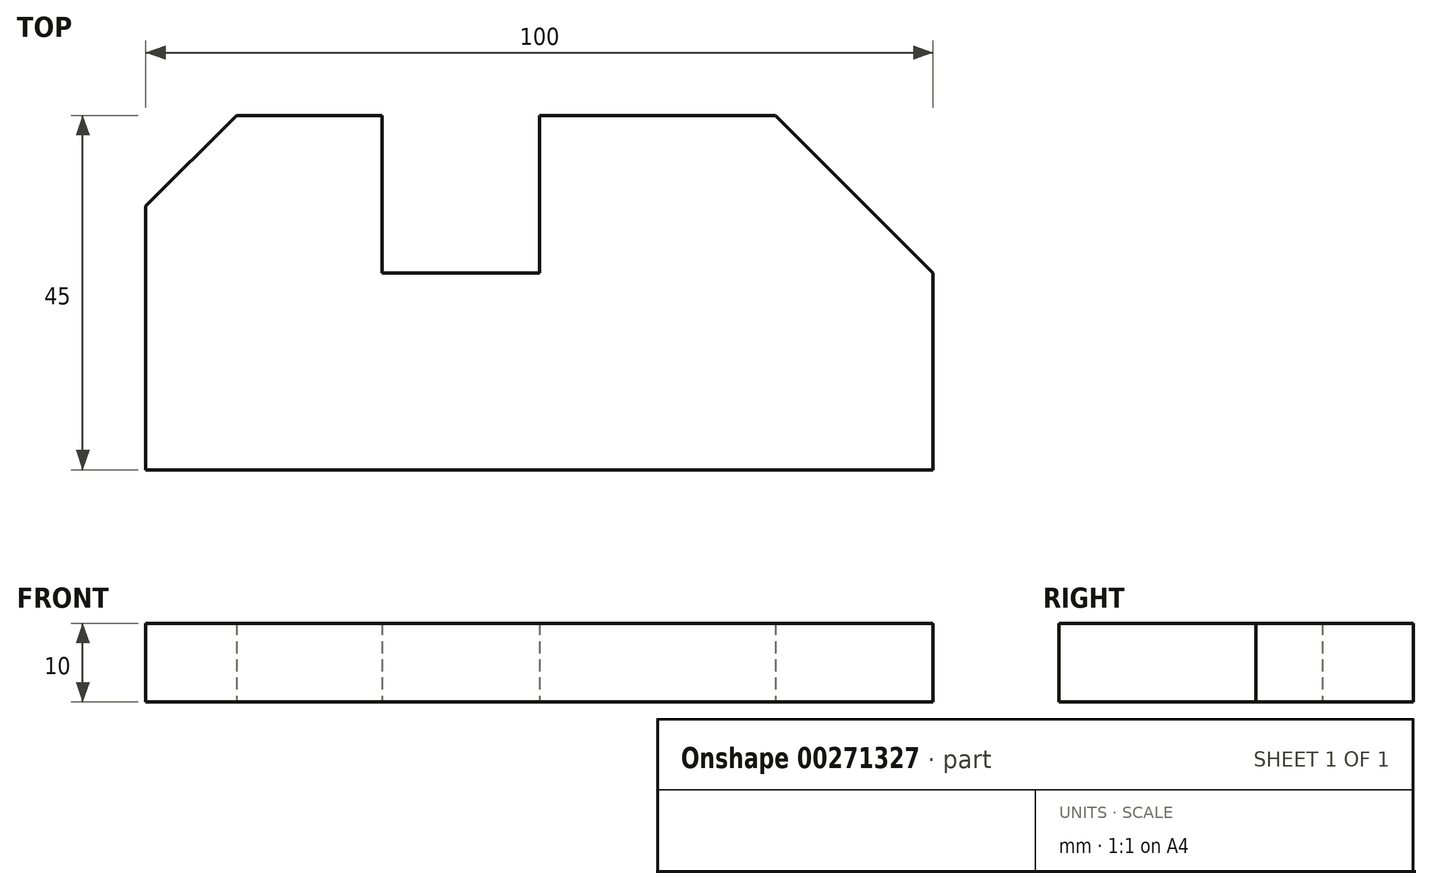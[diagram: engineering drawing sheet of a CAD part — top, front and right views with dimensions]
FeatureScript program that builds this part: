
annotation { "Feature Type Name" : "Feature", "Feature Type Description" : "" }
export const myFeature = defineFeature(function(context is Context, id is Id, definition is map)
    precondition{}
    {
        {
            var Q0;
            Q0=qCreatedBy(makeId("Top.planeOp"),FACE);
            var sketch = newSketch(context, id + "F0", { "sketchPlane" : qUnion([Q0])});
            skLineSegment(sketch, "E0", {"start": v(0, 0) * mm, "end": v(100, 0) * mm});
            skLineSegment(sketch, "E1", {"start": v(0, 0) * mm, "end": v(0, 33.48) * mm});
            skLineSegment(sketch, "E2", {"start": v(0, 33.48) * mm, "end": v(11.52, 45) * mm});
            skLineSegment(sketch, "E3", {"start": v(11.52, 45) * mm, "end": v(30, 45) * mm});
            skLineSegment(sketch, "E4", {"start": v(30, 45) * mm, "end": v(30, 25) * mm});
            skLineSegment(sketch, "E5", {"start": v(30, 25) * mm, "end": v(50, 25) * mm});
            skLineSegment(sketch, "E6", {"start": v(50, 25) * mm, "end": v(50, 45) * mm});
            skLineSegment(sketch, "E7", {"start": v(50, 45) * mm, "end": v(80, 45) * mm});
            skLineSegment(sketch, "E8", {"start": v(80, 45) * mm, "end": v(100, 25) * mm});
            skLineSegment(sketch, "E9", {"start": v(100, 25) * mm, "end": v(100, 0) * mm});
            skSolve(sketch);
        }
        {
            var Q0;
            Q0=makeQuery(id+"F0.imprint","IMPRINT",FACE,{"disambiguationData":[TD([[makeQuery(id+"F0.imprint","IMPRINT",EDGE,{"derivedFrom":sQuery(id+"F0.wireOp",EDGE,"E0")}),1.0]])]});
            extrude(context, id + "F1", {"entities" : qUnion([Q0]), "depth" : 10 * mm});
        }
    });
